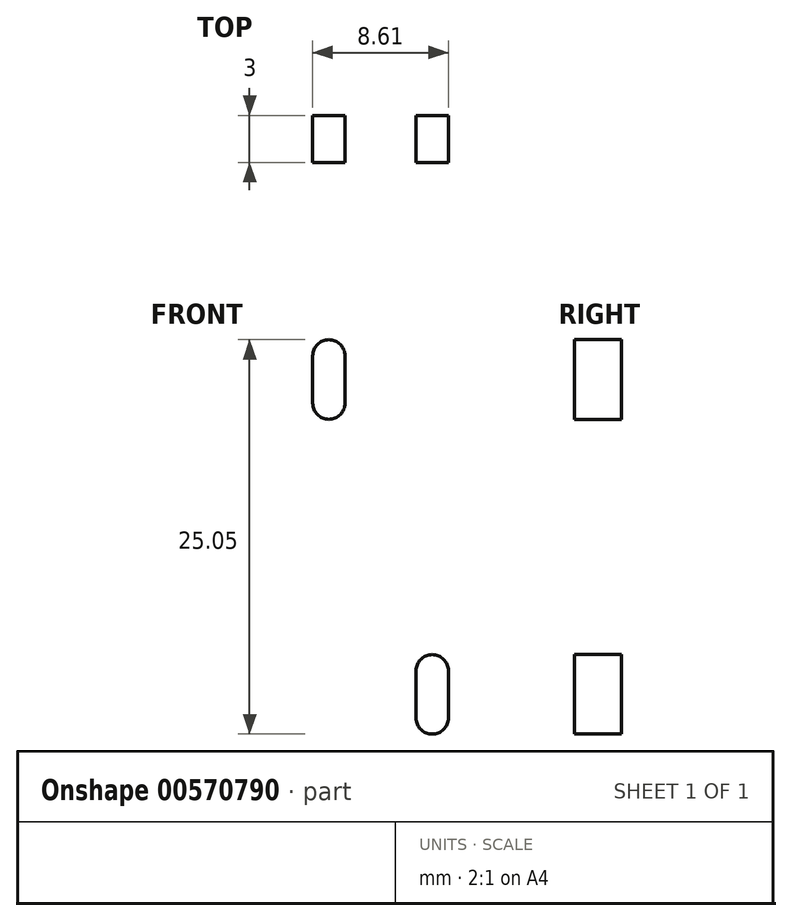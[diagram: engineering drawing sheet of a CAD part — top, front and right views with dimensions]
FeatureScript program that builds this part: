
annotation { "Feature Type Name" : "Feature", "Feature Type Description" : "" }
export const myFeature = defineFeature(function(context is Context, id is Id, definition is map)
    precondition{}
    {
        {
            var Q0;
            Q0=qCreatedBy(makeId("Front.planeOp"),FACE);
            var sketch = newSketch(context, id + "F0", { "sketchPlane" : qUnion([Q0])});
            skLineSegment(sketch, "E0.bottom", {"start": v(-21.56, 37.49) * mm, "end": v(-6.56, 37.49) * mm});
            skLineSegment(sketch, "E1", {"start": v(-21.56, 37.49) * mm, "end": v(-6.56, -37.51) * mm, "construction": true});
            skLineSegment(sketch, "E2", {"start": v(-14.06, -0.01) * mm, "end": v(-16.02, -0.4) * mm, "construction": true});
            skPoint(sketch, "E0.left.end.orphan", {"position": v(-21.56, -37.51) * mm});
            skLineSegment(sketch, "E3", {"start": v(-6.56, -37.51) * mm, "end": v(-6.56, 37.49) * mm, "construction": true});
            skPoint(sketch, "E0.right.start.orphan", {"position": v(8.44, 37.49) * mm});
            skPoint(sketch, "E0.top.end.orphan", {"position": v(8.44, -37.51) * mm});
            skFitSpline(sketch, "E4", {"points": [v(-21.56, 37.49) * mm, v(-16.02, -0.4) * mm, v(-6.56, -37.51) * mm], "startDerivative": vector(9.12, -76.18) * mm, "endDerivative": vector(20.88, -73.82) * mm});
            skLineSegment(sketch, "E5.MirrorCS", {"start": v(0.94, -0.01) * mm, "end": v(2.9, -0.4) * mm, "construction": true});
            skFitSpline(sketch, "E6.MirrorCS", {"points": [v(8.44, 37.49) * mm, v(2.9, -0.4) * mm, v(-6.56, -37.51) * mm], "startDerivative": vector(-9.12, -76.18) * mm, "endDerivative": vector(-20.88, -73.82) * mm});
            skLineSegment(sketch, "E7.MirrorCS", {"start": v(8.44, 37.49) * mm, "end": v(-6.56, 37.49) * mm});
            skLineSegment(sketch, "E8.MirrorCS", {"start": v(8.44, 37.49) * mm, "end": v(-6.56, -37.51) * mm, "construction": true});
            skSolve(sketch);
        }
        {
            var Q0;
            Q0=makeQuery(id+"F0.imprint","IMPRINT",FACE,{"disambiguationData":[TD([[makeQuery(id+"F0.imprint","IMPRINT",EDGE,{"derivedFrom":sQuery(id+"F0.wireOp",EDGE,"E0.bottom")}),-1.0]])]});
            extrude(context, id + "F1", {"entities" : qUnion([Q0]), "depth" : 3 * mm, "offsetDistance" : 25 * mm});
        }
        {
            var Q0;
            Q0=makeQuery(id+"F1.opExtrude","CAP_FACE",FACE,{"disambiguationData":[OSD([sQuery(id+"F0.wireOp",EDGE,"E0.bottom"),sQuery(id+"F0.wireOp",EDGE,"E4"),sQuery(id+"F0.wireOp",EDGE,"E6.MirrorCS"),sQuery(id+"F0.wireOp",EDGE,"E7.MirrorCS")])],"isStart":true});
            var sketch = newSketch(context, id + "F2", { "sketchPlane" : qUnion([Q0])});
            skLineSegment(sketch, "E9", {"start": v(-8.44, 37.49) * mm, "end": v(6.56, 37.49) * mm, "construction": true});
            skLineSegment(sketch, "E10", {"start": v(0, 37.49) * mm, "end": v(0, 17.49) * mm, "construction": true});
            skLineSegment(sketch, "E11", {"start": v(0, 16.46) * mm, "end": v(1.03, 16.46) * mm, "construction": true});
            skLineSegment(sketch, "E12", {"start": v(1.02, 16.46) * mm, "end": v(1.03, 13.46) * mm});
            skLineSegment(sketch, "E13", {"start": v(1.03, 13.46) * mm, "end": v(-1.02, 13.46) * mm, "construction": true});
            skLineSegment(sketch, "E14", {"start": v(-1.02, 13.46) * mm, "end": v(-1.02, 16.46) * mm});
            skLineSegment(sketch, "E15", {"start": v(-1.02, 16.46) * mm, "end": v(0, 16.46) * mm, "construction": true});
            skArc(sketch, "E16", {"start": v(1.02, 16.46) * mm, "mid": v(0, 17.49) * mm, "end": v(-1.02, 16.46) * mm});
            skArc(sketch, "E17", {"start": v(-1.02, 13.46) * mm, "mid": v(0, 12.44) * mm, "end": v(1.03, 13.46) * mm});
            skLineSegment(sketch, "E18.trimOffspring", {"start": v(0, 13.46) * mm, "end": v(0, 12.44) * mm, "construction": true});
            skLineSegment(sketch, "E19", {"start": v(6.56, 37.49) * mm, "end": v(6.56, -2.51) * mm, "construction": true});
            skArc(sketch, "E20.MirrorCS", {"start": v(12.1, 16.46) * mm, "mid": v(13.13, 17.49) * mm, "end": v(14.15, 16.46) * mm});
            skLineSegment(sketch, "E21.MirrorCS", {"start": v(14.15, 16.46) * mm, "end": v(13.13, 16.46) * mm, "construction": true});
            skArc(sketch, "E22.MirrorCS", {"start": v(14.15, 13.46) * mm, "mid": v(13.13, 12.44) * mm, "end": v(12.1, 13.46) * mm});
            skLineSegment(sketch, "E23.MirrorCS", {"start": v(13.13, 13.46) * mm, "end": v(13.13, 12.44) * mm, "construction": true});
            skLineSegment(sketch, "E24.MirrorCS", {"start": v(21.56, 37.49) * mm, "end": v(6.56, 37.49) * mm, "construction": true});
            skLineSegment(sketch, "E25.MirrorCS", {"start": v(13.13, 37.49) * mm, "end": v(13.13, 17.49) * mm, "construction": true});
            skLineSegment(sketch, "E26.MirrorCS", {"start": v(12.1, 13.46) * mm, "end": v(14.15, 13.46) * mm, "construction": true});
            skLineSegment(sketch, "E27.MirrorCS", {"start": v(13.13, 16.46) * mm, "end": v(12.1, 16.46) * mm, "construction": true});
            skLineSegment(sketch, "E28.MirrorCS", {"start": v(12.1, 16.46) * mm, "end": v(12.1, 13.46) * mm});
            skLineSegment(sketch, "E29.MirrorCS", {"start": v(14.15, 13.46) * mm, "end": v(14.15, 16.46) * mm});
            skArc(sketch, "E30.MirrorCS", {"start": v(5.54, -3.54) * mm, "mid": v(6.56, -2.51) * mm, "end": v(7.59, -3.54) * mm});
            skLineSegment(sketch, "E31.MirrorCS", {"start": v(7.59, -3.54) * mm, "end": v(6.56, -3.54) * mm, "construction": true});
            skArc(sketch, "E32.MirrorCS", {"start": v(7.59, -6.54) * mm, "mid": v(6.56, -7.56) * mm, "end": v(5.54, -6.54) * mm});
            skLineSegment(sketch, "E33.MirrorCS", {"start": v(6.56, -6.54) * mm, "end": v(6.56, -7.56) * mm, "construction": true});
            skLineSegment(sketch, "E34.MirrorCS", {"start": v(5.54, -6.54) * mm, "end": v(7.59, -6.54) * mm, "construction": true});
            skLineSegment(sketch, "E35.MirrorCS", {"start": v(6.56, -3.54) * mm, "end": v(5.54, -3.54) * mm, "construction": true});
            skLineSegment(sketch, "E36.MirrorCS", {"start": v(5.54, -3.54) * mm, "end": v(5.54, -6.54) * mm});
            skLineSegment(sketch, "E37.MirrorCS", {"start": v(7.59, -6.54) * mm, "end": v(7.59, -3.54) * mm});
            skSolve(sketch);
        }
        {
            var Q0;
            Q0=makeQuery(id+"F2.imprint","IMPRINT",FACE,{"disambiguationData":[TD([[makeQuery(id+"F2.imprint","IMPRINT",EDGE,{"derivedFrom":sQuery(id+"F2.wireOp",EDGE,"E12")}),-1.0]])]});
            var Q1;
            Q1=makeQuery(id+"F2.imprint","IMPRINT",FACE,{"disambiguationData":[TD([[makeQuery(id+"F2.imprint","IMPRINT",EDGE,{"derivedFrom":sQuery(id+"F2.wireOp",EDGE,"E20.MirrorCS")}),-1.0]])]});
            var Q2;
            Q2=makeQuery(id+"F2.imprint","IMPRINT",FACE,{"disambiguationData":[TD([[makeQuery(id+"F2.imprint","IMPRINT",EDGE,{"derivedFrom":sQuery(id+"F2.wireOp",EDGE,"E30.MirrorCS")}),-1.0]])]});
            extrude(context, id + "F3", {"entities" : qUnion([Q0, Q1, Q2]), "operationType" : NewBodyOperationType.REMOVE, "endBound" : BoundingType.UP_TO_NEXT, "oppositeDirection" : true, "depth" : 25 * mm, "offsetDistance" : 25 * mm});
        }
    });
